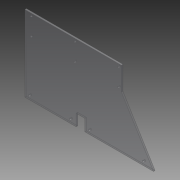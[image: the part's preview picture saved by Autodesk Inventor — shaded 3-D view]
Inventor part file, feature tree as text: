
AUTODESK INVENTOR PART (.ipt)
format: ipt  version: 2014 SP1 (Build 180222100, 222)  size: 102,912 bytes
history: native  units: in
note: dims shown in document units (in); Inventor stores cm internally (conversion verified against a paired STEP export)
features: reference x3, extrude x1, sketch x1
ambient origin geometry x8: Origin, YZ Plane, XZ Plane, XY Plane, X Axis, Y Axis, Z Axis, Center Point
bodies: Solid1 (feature_tree)
feature tree (5):
  extrude  "Extrusion1"  Depth=0.75in
  sketch  "Sketch1"  dims[d0=11.0in d1=6.5in d2=8.25in d3=2.0in d4=0.125in d5=0.0in d6=0.75in d7=1.0in d8=0.5in d9=0.125in d10=1.1811in d12=3.75in d13=0.7874in d15=1.5in d18=0.5in d19=0.25in]
  reference  "Reference1"
  reference  "Reference2"
  reference  "Reference3"
